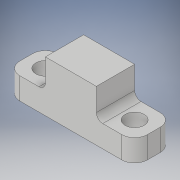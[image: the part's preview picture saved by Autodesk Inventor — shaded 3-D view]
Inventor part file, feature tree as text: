
AUTODESK INVENTOR PART (.ipt)
format: ipt  version: 2018 (Build 220112000, 112)  size: 132,608 bytes
history: native  units: in
note: dims shown in document units (in); Inventor stores cm internally (conversion verified against a paired STEP export)
features: sketch x3, extrude x2, fillet x2, mirror x1
ambient origin geometry x8: Origin, YZ Plane, XZ Plane, XY Plane, X Axis, Y Axis, Z Axis, Center Point
bodies: Solid1 (feature_tree)
feature tree (8):
  sketch  "Sketch1"  dims[d1=1.0in d3=0.75in d4=0.0in d5=0.25in d6=0.125in]
  extrude  "Extrusion1"  Depth=0.75in TaperAngle=0.0deg
  fillet  "Fillet1"  Radius=0.25in
  fillet  "Fillet2"  Radius=0.125in
  extrude  "Extrusion2"  Depth=0.375in
  mirror  "Mirror1"
  sketch  "Sketch2"  dims[d7=0.375in d8=0.375in]
  sketch  "Sketch3"  dims[d9=0.375in d10=0.75in d11=0.0in]
